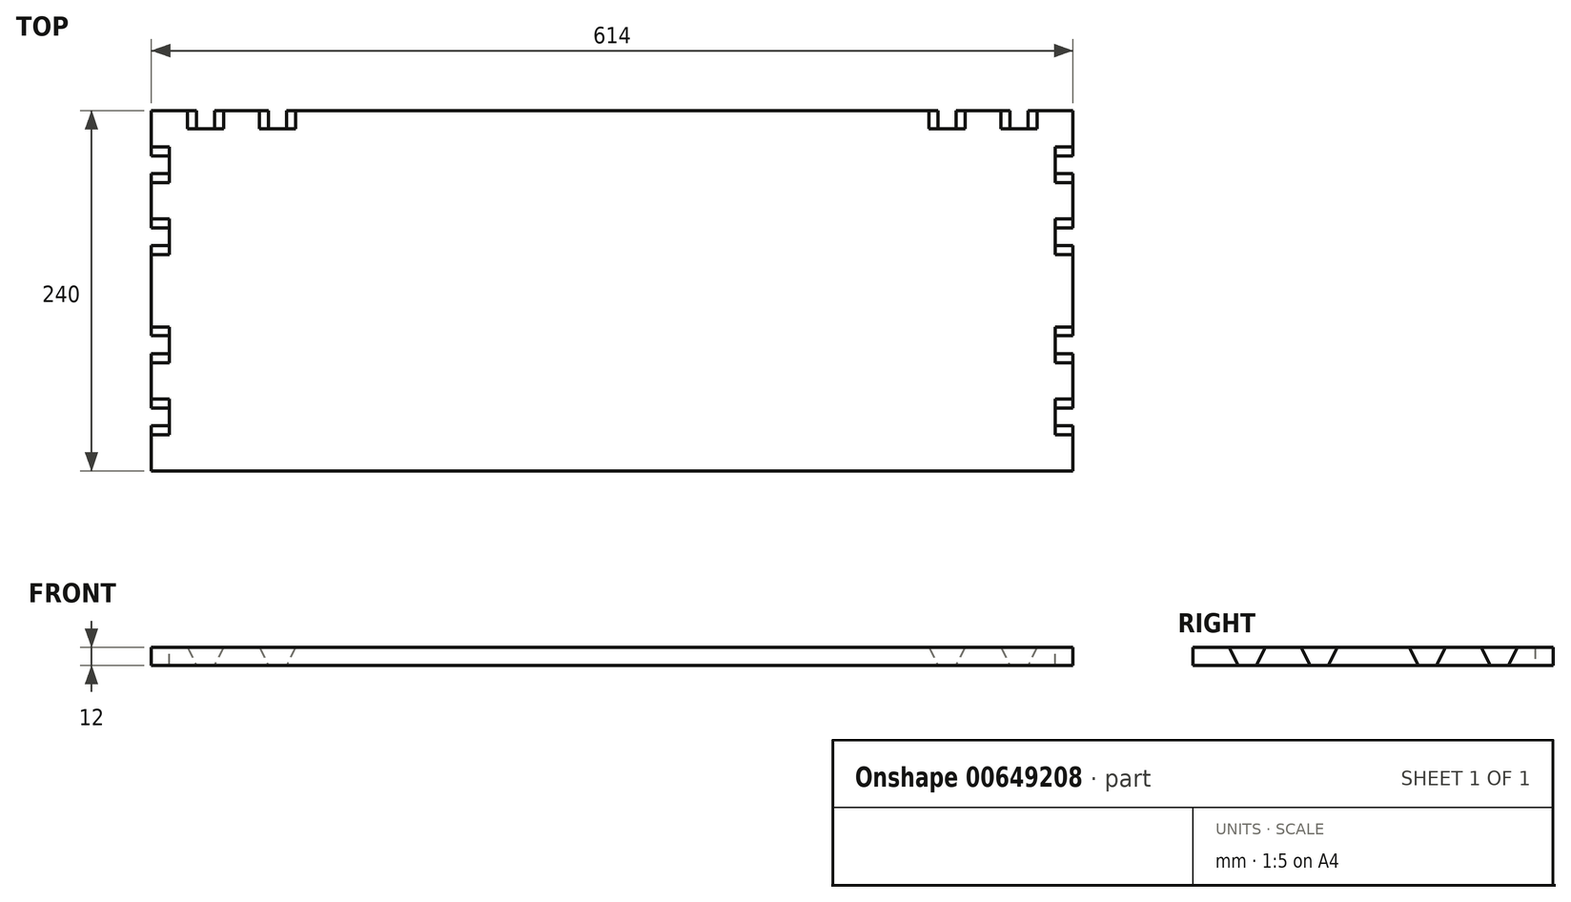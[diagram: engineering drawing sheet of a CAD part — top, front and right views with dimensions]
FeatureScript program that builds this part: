
annotation { "Feature Type Name" : "Feature", "Feature Type Description" : "" }
export const myFeature = defineFeature(function(context is Context, id is Id, definition is map)
    precondition{}
    {
        {
            var Q0;
            Q0=qCreatedBy(makeId("Top.planeOp"),FACE);
            var sketch = newSketch(context, id + "F0", { "sketchPlane" : qUnion([Q0])});
            skLineSegment(sketch, "E0.bottom", {"start": v(-307, 120) * mm, "end": v(307, 120) * mm});
            skLineSegment(sketch, "E0.top", {"start": v(-307, -120) * mm, "end": v(307, -120) * mm});
            skLineSegment(sketch, "E0.left", {"start": v(-307, 120) * mm, "end": v(-307, -120) * mm});
            skLineSegment(sketch, "E0.right", {"start": v(307, 120) * mm, "end": v(307, -120) * mm});
            skPoint(sketch, "E0.middle", {"position": v(0, 0) * mm});
            skLineSegment(sketch, "E1", {"start": v(-295, 120) * mm, "end": v(-295, -120) * mm, "construction": true});
            skLineSegment(sketch, "E2", {"start": v(-295, 116.5) * mm, "end": v(-307, 116.5) * mm, "construction": true});
            skLineSegment(sketch, "E3", {"start": v(295, 120) * mm, "end": v(295, -120) * mm, "construction": true});
            skLineSegment(sketch, "E4", {"start": v(307, 108.53) * mm, "end": v(295, 108.53) * mm, "construction": true});
            skLineSegment(sketch, "E5", {"start": v(-307, 108) * mm, "end": v(307, 108) * mm, "construction": true});
            skLineSegment(sketch, "E6", {"start": v(-289.12, 120) * mm, "end": v(-289.12, 108) * mm, "construction": true});
            skLineSegment(sketch, "E7.bottom", {"start": v(-307, -72) * mm, "end": v(-295, -72) * mm});
            skLineSegment(sketch, "E7.top", {"start": v(-307, -96) * mm, "end": v(-295, -96) * mm});
            skLineSegment(sketch, "E7.left", {"start": v(-307, -72) * mm, "end": v(-307, -96) * mm});
            skLineSegment(sketch, "E7.right", {"start": v(-295, -72) * mm, "end": v(-295, -96) * mm});
            skPoint(sketch, "E8", {"position": v(-307, -72) * mm});
            skPoint(sketch, "E9", {"position": v(-307, -96) * mm});
            skLineSegment(sketch, "E10", {"start": v(-301, -96) * mm, "end": v(-301, -120) * mm, "construction": true});
            skLineSegment(sketch, "E11", {"start": v(-307, -48) * mm, "end": v(-295, -48) * mm});
            skLineSegment(sketch, "E12", {"start": v(-295, -48) * mm, "end": v(-295, -24) * mm});
            skLineSegment(sketch, "E13", {"start": v(-295, -24) * mm, "end": v(-307, -24) * mm});
            skLineSegment(sketch, "E14", {"start": v(-307, -24) * mm, "end": v(-307, -48) * mm});
            skLineSegment(sketch, "E15", {"start": v(-301, -48) * mm, "end": v(-301, -72) * mm, "construction": true});
            skLineSegment(sketch, "E16", {"start": v(-307, 48) * mm, "end": v(-295, 48) * mm});
            skLineSegment(sketch, "E17", {"start": v(-295, 48) * mm, "end": v(-295, 24) * mm});
            skLineSegment(sketch, "E18", {"start": v(-295, 24) * mm, "end": v(-307, 24) * mm});
            skLineSegment(sketch, "E19", {"start": v(-307, 24) * mm, "end": v(-307, 48) * mm});
            skLineSegment(sketch, "E20.bottom", {"start": v(-307, 96) * mm, "end": v(-295, 96) * mm});
            skLineSegment(sketch, "E20.top", {"start": v(-307, 72) * mm, "end": v(-295, 72) * mm});
            skLineSegment(sketch, "E20.left", {"start": v(-307, 96) * mm, "end": v(-307, 72) * mm});
            skLineSegment(sketch, "E20.right", {"start": v(-295, 96) * mm, "end": v(-295, 72) * mm});
            skLineSegment(sketch, "E21", {"start": v(-301, 72) * mm, "end": v(-301, 48) * mm, "construction": true});
            skPoint(sketch, "E22.startSnap0", {"position": v(-301, 116.5) * mm});
            skLineSegment(sketch, "E23", {"start": v(-300.8, 120) * mm, "end": v(-300.8, 96) * mm, "construction": true});
            skLineSegment(sketch, "E24.bottom", {"start": v(295, -96) * mm, "end": v(307, -96) * mm});
            skLineSegment(sketch, "E24.top", {"start": v(295, -72) * mm, "end": v(307, -72) * mm});
            skLineSegment(sketch, "E24.left", {"start": v(295, -96) * mm, "end": v(295, -72) * mm});
            skLineSegment(sketch, "E24.right", {"start": v(307, -96) * mm, "end": v(307, -72) * mm});
            skLineSegment(sketch, "E25.bottom", {"start": v(295, -48) * mm, "end": v(307, -48) * mm});
            skLineSegment(sketch, "E25.top", {"start": v(295, -24) * mm, "end": v(307, -24) * mm});
            skLineSegment(sketch, "E25.left", {"start": v(295, -48) * mm, "end": v(295, -24) * mm});
            skLineSegment(sketch, "E25.right", {"start": v(307, -48) * mm, "end": v(307, -24) * mm});
            skLineSegment(sketch, "E26.bottom", {"start": v(295, 96) * mm, "end": v(307, 96) * mm});
            skLineSegment(sketch, "E26.top", {"start": v(295, 72) * mm, "end": v(307, 72) * mm});
            skLineSegment(sketch, "E26.left", {"start": v(295, 96) * mm, "end": v(295, 72) * mm});
            skLineSegment(sketch, "E26.right", {"start": v(307, 96) * mm, "end": v(307, 72) * mm});
            skLineSegment(sketch, "E27.bottom", {"start": v(295, 48) * mm, "end": v(307, 48) * mm});
            skLineSegment(sketch, "E27.top", {"start": v(295, 24) * mm, "end": v(307, 24) * mm});
            skLineSegment(sketch, "E27.left", {"start": v(295, 48) * mm, "end": v(295, 24) * mm});
            skLineSegment(sketch, "E27.right", {"start": v(307, 48) * mm, "end": v(307, 24) * mm});
            skLineSegment(sketch, "E28", {"start": v(301, -96) * mm, "end": v(301, -120) * mm, "construction": true});
            skLineSegment(sketch, "E29", {"start": v(300.92, 120) * mm, "end": v(300.92, 96) * mm, "construction": true});
            skLineSegment(sketch, "E30", {"start": v(301, -48) * mm, "end": v(301, -72) * mm, "construction": true});
            skLineSegment(sketch, "E31", {"start": v(301, 72) * mm, "end": v(301, 48) * mm, "construction": true});
            skLineSegment(sketch, "E32.bottom", {"start": v(-283, 120) * mm, "end": v(-259, 120) * mm});
            skLineSegment(sketch, "E32.top", {"start": v(-283, 108) * mm, "end": v(-259, 108) * mm});
            skLineSegment(sketch, "E32.left", {"start": v(-283, 120) * mm, "end": v(-283, 108) * mm});
            skLineSegment(sketch, "E32.right", {"start": v(-259, 120) * mm, "end": v(-259, 108) * mm});
            skLineSegment(sketch, "E33.bottom", {"start": v(-235, 120) * mm, "end": v(-211, 120) * mm});
            skLineSegment(sketch, "E33.top", {"start": v(-235, 108) * mm, "end": v(-211, 108) * mm});
            skLineSegment(sketch, "E33.left", {"start": v(-235, 120) * mm, "end": v(-235, 108) * mm});
            skLineSegment(sketch, "E33.right", {"start": v(-211, 120) * mm, "end": v(-211, 108) * mm});
            skLineSegment(sketch, "E34.bottom", {"start": v(283, 120) * mm, "end": v(259, 120) * mm});
            skLineSegment(sketch, "E34.top", {"start": v(283, 108) * mm, "end": v(259, 108) * mm});
            skLineSegment(sketch, "E34.left", {"start": v(283, 120) * mm, "end": v(283, 108) * mm});
            skLineSegment(sketch, "E34.right", {"start": v(259, 120) * mm, "end": v(259, 108) * mm});
            skLineSegment(sketch, "E35.bottom", {"start": v(235, 120) * mm, "end": v(211, 120) * mm});
            skLineSegment(sketch, "E35.top", {"start": v(235, 108) * mm, "end": v(211, 108) * mm});
            skLineSegment(sketch, "E35.left", {"start": v(235, 120) * mm, "end": v(235, 108) * mm});
            skLineSegment(sketch, "E35.right", {"start": v(211, 120) * mm, "end": v(211, 108) * mm});
            skLineSegment(sketch, "E36", {"start": v(307, 114.86) * mm, "end": v(283, 114.86) * mm, "construction": true});
            skLineSegment(sketch, "E37", {"start": v(259, 114) * mm, "end": v(235, 114) * mm, "construction": true});
            skLineSegment(sketch, "E38", {"start": v(-307, 113.75) * mm, "end": v(-283, 113.75) * mm, "construction": true});
            skLineSegment(sketch, "E39", {"start": v(-259, 114) * mm, "end": v(-235, 114) * mm, "construction": true});
            skLineSegment(sketch, "E40", {"start": v(-235, 111.04) * mm, "end": v(-211, 111.04) * mm, "construction": true});
            skLineSegment(sketch, "E41", {"start": v(235, 110.72) * mm, "end": v(211, 110.72) * mm, "construction": true});
            skLineSegment(sketch, "E42", {"start": v(259, 111.01) * mm, "end": v(283, 111.01) * mm, "construction": true});
            skSolve(sketch);
        }
        {
            var Q0;
            {var subQ4=sQuery(id+"F0.wireOp",EDGE,"E0.bottom");Q0=makeQuery(id+"F0.imprint","IMPRINT",FACE,{"disambiguationData":[TD([[makeQuery(id+"F0.imprint","IMPRINT",EDGE,{"derivedFrom":subQ4}),-1.0]])]});}
            extrude(context, id + "F1", {"entities" : qUnion([Q0]), "depth" : 12 * mm, "offsetDistance" : 25 * mm});
        }
        {
            var Q0;
            Q0=makeQuery(id+"F1.opExtrude","SWEPT_FACE",FACE,{"disambiguationData":[OSD([sQuery(id+"F0.wireOp",EDGE,"E7.right")])]});
            var sketch = newSketch(context, id + "F2", { "sketchPlane" : qUnion([Q0])});
            skLineSegment(sketch, "E43", {"start": v(72, 12) * mm, "end": v(72, 0) * mm});
            skLineSegment(sketch, "E44", {"start": v(72, 0) * mm, "end": v(78, 0) * mm});
            skLineSegment(sketch, "E45", {"start": v(78, 0) * mm, "end": v(72, 12) * mm});
            skLineSegment(sketch, "E46", {"start": v(96, 12) * mm, "end": v(96, 0) * mm});
            skLineSegment(sketch, "E47", {"start": v(96, 0) * mm, "end": v(90, 0) * mm});
            skLineSegment(sketch, "E48", {"start": v(90, 0) * mm, "end": v(96, 12) * mm});
            skSolve(sketch);
        }
        {
            var Q0;
            Q0 = qSketchRegion(id + "F2", true);
            extrude(context, id + "F3", {"entities" : qUnion([Q0]), "operationType" : NewBodyOperationType.ADD, "depth" : 12 * mm, "offsetDistance" : 25 * mm});
        }
        {
            var Q0;
            Q0=makeQuery(id+"F1.opExtrude","SWEPT_FACE",FACE,{"disambiguationData":[OSD([sQuery(id+"F0.wireOp",EDGE,"E12")])]});
            var sketch = newSketch(context, id + "F4", { "sketchPlane" : qUnion([Q0])});
            skLineSegment(sketch, "E49", {"start": v(24, 12) * mm, "end": v(30, 0) * mm});
            skLineSegment(sketch, "E50", {"start": v(30, 0) * mm, "end": v(24, 0) * mm});
            skLineSegment(sketch, "E51", {"start": v(24, 0) * mm, "end": v(24, 12) * mm});
            skLineSegment(sketch, "E52", {"start": v(48, 12) * mm, "end": v(48, 0) * mm});
            skLineSegment(sketch, "E53", {"start": v(48, 0) * mm, "end": v(42, 0) * mm});
            skLineSegment(sketch, "E54", {"start": v(42, 0) * mm, "end": v(48, 12) * mm});
            skSolve(sketch);
        }
        {
            var Q0;
            Q0 = qSketchRegion(id + "F4", true);
            extrude(context, id + "F5", {"entities" : qUnion([Q0]), "operationType" : NewBodyOperationType.ADD, "depth" : 12 * mm, "offsetDistance" : 25 * mm});
        }
        {
            var Q0;
            Q0=makeQuery(id+"F1.opExtrude","SWEPT_FACE",FACE,{"disambiguationData":[OSD([sQuery(id+"F0.wireOp",EDGE,"E17")])]});
            var sketch = newSketch(context, id + "F6", { "sketchPlane" : qUnion([Q0])});
            skLineSegment(sketch, "E55", {"start": v(-48, 12) * mm, "end": v(-42, 0) * mm});
            skLineSegment(sketch, "E56", {"start": v(-42, 0) * mm, "end": v(-48, 0) * mm});
            skLineSegment(sketch, "E57", {"start": v(-48, 0) * mm, "end": v(-48, 12) * mm});
            skLineSegment(sketch, "E58", {"start": v(-24, 12) * mm, "end": v(-24, 0) * mm});
            skLineSegment(sketch, "E59", {"start": v(-24, 0) * mm, "end": v(-30, 0) * mm});
            skLineSegment(sketch, "E60", {"start": v(-30, 0) * mm, "end": v(-24, 12) * mm});
            skSolve(sketch);
        }
        {
            var Q0;
            Q0 = qSketchRegion(id + "F6", true);
            extrude(context, id + "F7", {"entities" : qUnion([Q0]), "operationType" : NewBodyOperationType.ADD, "depth" : 12 * mm, "offsetDistance" : 25 * mm});
        }
        {
            var Q0;
            Q0=makeQuery(id+"F1.opExtrude","SWEPT_FACE",FACE,{"disambiguationData":[OSD([sQuery(id+"F0.wireOp",EDGE,"E20.right")])]});
            var sketch = newSketch(context, id + "F8", { "sketchPlane" : qUnion([Q0])});
            skLineSegment(sketch, "E61", {"start": v(-96, 12) * mm, "end": v(-90, 0) * mm});
            skLineSegment(sketch, "E62", {"start": v(-90, 0) * mm, "end": v(-96, 0) * mm});
            skLineSegment(sketch, "E63", {"start": v(-96, 0) * mm, "end": v(-96, 12) * mm});
            skLineSegment(sketch, "E64", {"start": v(-72, 12) * mm, "end": v(-72, 0) * mm});
            skLineSegment(sketch, "E65", {"start": v(-72, 0) * mm, "end": v(-78, 0) * mm});
            skLineSegment(sketch, "E66", {"start": v(-78, 0) * mm, "end": v(-72, 12) * mm});
            skSolve(sketch);
        }
        {
            var Q0;
            Q0 = qSketchRegion(id + "F8", true);
            extrude(context, id + "F9", {"entities" : qUnion([Q0]), "operationType" : NewBodyOperationType.ADD, "depth" : 12 * mm, "offsetDistance" : 25 * mm});
        }
        {
            var Q0;
            Q0=makeQuery(id+"F1.opExtrude","SWEPT_FACE",FACE,{"disambiguationData":[OSD([sQuery(id+"F0.wireOp",EDGE,"E24.left")])]});
            var sketch = newSketch(context, id + "F10", { "sketchPlane" : qUnion([Q0])});
            skLineSegment(sketch, "E67", {"start": v(-96, 12) * mm, "end": v(-90, 0) * mm});
            skLineSegment(sketch, "E68", {"start": v(-90, 0) * mm, "end": v(-96, 0) * mm});
            skLineSegment(sketch, "E69", {"start": v(-96, 0) * mm, "end": v(-96, 12) * mm});
            skLineSegment(sketch, "E70", {"start": v(-72, 12) * mm, "end": v(-72, 0) * mm});
            skLineSegment(sketch, "E71", {"start": v(-72, 0) * mm, "end": v(-78, 0) * mm});
            skLineSegment(sketch, "E72", {"start": v(-78, 0) * mm, "end": v(-72, 12) * mm});
            skSolve(sketch);
        }
        {
            var Q0;
            Q0 = qSketchRegion(id + "F10", true);
            extrude(context, id + "F11", {"entities" : qUnion([Q0]), "operationType" : NewBodyOperationType.ADD, "depth" : 12 * mm, "offsetDistance" : 25 * mm});
        }
        {
            var Q0;
            Q0=makeQuery(id+"F1.opExtrude","SWEPT_FACE",FACE,{"disambiguationData":[OSD([sQuery(id+"F0.wireOp",EDGE,"E25.left")])]});
            var sketch = newSketch(context, id + "F12", { "sketchPlane" : qUnion([Q0])});
            skLineSegment(sketch, "E73", {"start": v(-48, 12) * mm, "end": v(-42, 0) * mm});
            skLineSegment(sketch, "E74", {"start": v(-42, 0) * mm, "end": v(-48, 0) * mm});
            skLineSegment(sketch, "E75", {"start": v(-48, 0) * mm, "end": v(-48, 12) * mm});
            skLineSegment(sketch, "E76", {"start": v(-24, 12) * mm, "end": v(-24, 0) * mm});
            skLineSegment(sketch, "E77", {"start": v(-24, 0) * mm, "end": v(-30, 0) * mm});
            skLineSegment(sketch, "E78", {"start": v(-30, 0) * mm, "end": v(-24, 12) * mm});
            skSolve(sketch);
        }
        {
            var Q0;
            Q0 = qSketchRegion(id + "F12", true);
            extrude(context, id + "F13", {"entities" : qUnion([Q0]), "operationType" : NewBodyOperationType.ADD, "depth" : 12 * mm, "offsetDistance" : 25 * mm});
        }
        {
            var Q0;
            Q0=makeQuery(id+"F1.opExtrude","SWEPT_FACE",FACE,{"disambiguationData":[OSD([sQuery(id+"F0.wireOp",EDGE,"E27.left")])]});
            var sketch = newSketch(context, id + "F14", { "sketchPlane" : qUnion([Q0])});
            skLineSegment(sketch, "E79", {"start": v(24, 12) * mm, "end": v(30, 0) * mm});
            skLineSegment(sketch, "E80", {"start": v(30, 0) * mm, "end": v(24, 0) * mm});
            skLineSegment(sketch, "E81", {"start": v(24, 0) * mm, "end": v(24, 12) * mm});
            skLineSegment(sketch, "E82", {"start": v(48, 12) * mm, "end": v(48, 0) * mm});
            skLineSegment(sketch, "E83", {"start": v(48, 0) * mm, "end": v(42, 0) * mm});
            skLineSegment(sketch, "E84", {"start": v(42, 0) * mm, "end": v(48, 12) * mm});
            skSolve(sketch);
        }
        {
            var Q0;
            Q0 = qSketchRegion(id + "F14", true);
            extrude(context, id + "F15", {"entities" : qUnion([Q0]), "operationType" : NewBodyOperationType.ADD, "depth" : 12 * mm, "offsetDistance" : 25 * mm});
        }
        {
            var Q0;
            Q0=makeQuery(id+"F1.opExtrude","SWEPT_FACE",FACE,{"disambiguationData":[OSD([sQuery(id+"F0.wireOp",EDGE,"E26.left")])]});
            var sketch = newSketch(context, id + "F16", { "sketchPlane" : qUnion([Q0])});
            skLineSegment(sketch, "E85", {"start": v(72, 12) * mm, "end": v(78, 0) * mm});
            skLineSegment(sketch, "E86", {"start": v(78, 0) * mm, "end": v(72, 0) * mm});
            skLineSegment(sketch, "E87", {"start": v(72, 0) * mm, "end": v(72, 12) * mm});
            skLineSegment(sketch, "E88", {"start": v(96, 12) * mm, "end": v(96, 0) * mm});
            skLineSegment(sketch, "E89", {"start": v(96, 0) * mm, "end": v(90, 0) * mm});
            skLineSegment(sketch, "E90", {"start": v(90, 0) * mm, "end": v(96, 12) * mm});
            skSolve(sketch);
        }
        {
            var Q0;
            Q0 = qSketchRegion(id + "F16", true);
            extrude(context, id + "F17", {"entities" : qUnion([Q0]), "operationType" : NewBodyOperationType.ADD, "depth" : 12 * mm, "offsetDistance" : 25 * mm});
        }
        {
            var Q0;
            Q0=makeQuery(id+"F1.opExtrude","SWEPT_FACE",FACE,{"disambiguationData":[OSD([sQuery(id+"F0.wireOp",EDGE,"E34.top")])]});
            var sketch = newSketch(context, id + "F18", { "sketchPlane" : qUnion([Q0])});
            skLineSegment(sketch, "E91", {"start": v(-283, 12) * mm, "end": v(-277, 0) * mm});
            skLineSegment(sketch, "E92", {"start": v(-277, 0) * mm, "end": v(-283, 0) * mm});
            skLineSegment(sketch, "E93", {"start": v(-283, 0) * mm, "end": v(-283, 12) * mm});
            skLineSegment(sketch, "E94", {"start": v(-259, 12) * mm, "end": v(-265, 0) * mm});
            skLineSegment(sketch, "E95", {"start": v(-265, 0) * mm, "end": v(-259, 0) * mm});
            skLineSegment(sketch, "E96", {"start": v(-259, 0) * mm, "end": v(-259, 12) * mm});
            skSolve(sketch);
        }
        {
            var Q0;
            Q0 = qSketchRegion(id + "F18", true);
            extrude(context, id + "F19", {"entities" : qUnion([Q0]), "operationType" : NewBodyOperationType.ADD, "depth" : 12 * mm, "offsetDistance" : 25 * mm});
        }
        {
            var Q0;
            Q0=makeQuery(id+"F1.opExtrude","SWEPT_FACE",FACE,{"disambiguationData":[OSD([sQuery(id+"F0.wireOp",EDGE,"E35.top")])]});
            var sketch = newSketch(context, id + "F20", { "sketchPlane" : qUnion([Q0])});
            skLineSegment(sketch, "E97", {"start": v(-235, 12) * mm, "end": v(-229, 0) * mm});
            skLineSegment(sketch, "E98", {"start": v(-229, 0) * mm, "end": v(-235, 0) * mm});
            skLineSegment(sketch, "E99", {"start": v(-235, 0) * mm, "end": v(-235, 12) * mm});
            skLineSegment(sketch, "E100", {"start": v(-211, 12) * mm, "end": v(-217, 0) * mm});
            skLineSegment(sketch, "E101", {"start": v(-217, 0) * mm, "end": v(-211, 0) * mm});
            skLineSegment(sketch, "E102", {"start": v(-211, 0) * mm, "end": v(-211, 12) * mm});
            skSolve(sketch);
        }
        {
            var Q0;
            Q0 = qSketchRegion(id + "F20", true);
            extrude(context, id + "F21", {"entities" : qUnion([Q0]), "operationType" : NewBodyOperationType.ADD, "depth" : 12 * mm, "offsetDistance" : 25 * mm});
        }
        {
            var Q0;
            Q0=makeQuery(id+"F1.opExtrude","SWEPT_FACE",FACE,{"disambiguationData":[OSD([sQuery(id+"F0.wireOp",EDGE,"E33.top")])]});
            var sketch = newSketch(context, id + "F22", { "sketchPlane" : qUnion([Q0])});
            skLineSegment(sketch, "E103", {"start": v(211, 12) * mm, "end": v(217, 0) * mm});
            skLineSegment(sketch, "E104", {"start": v(217, 0) * mm, "end": v(211, 0) * mm});
            skLineSegment(sketch, "E105", {"start": v(211, 0) * mm, "end": v(211, 12) * mm});
            skLineSegment(sketch, "E106", {"start": v(235, 12) * mm, "end": v(229, 0) * mm});
            skLineSegment(sketch, "E107", {"start": v(229, 0) * mm, "end": v(235, 0) * mm});
            skLineSegment(sketch, "E108", {"start": v(235, 0) * mm, "end": v(235, 12) * mm});
            skSolve(sketch);
        }
        {
            var Q0;
            Q0 = qSketchRegion(id + "F22", true);
            extrude(context, id + "F23", {"entities" : qUnion([Q0]), "operationType" : NewBodyOperationType.ADD, "depth" : 12 * mm, "offsetDistance" : 25 * mm});
        }
        {
            var Q0;
            Q0=makeQuery(id+"F1.opExtrude","SWEPT_FACE",FACE,{"disambiguationData":[OSD([sQuery(id+"F0.wireOp",EDGE,"E32.top")])]});
            var sketch = newSketch(context, id + "F24", { "sketchPlane" : qUnion([Q0])});
            skLineSegment(sketch, "E109", {"start": v(259, 12) * mm, "end": v(265, 0) * mm});
            skLineSegment(sketch, "E110", {"start": v(265, 0) * mm, "end": v(259, 0) * mm});
            skLineSegment(sketch, "E111", {"start": v(259, 0) * mm, "end": v(259, 12) * mm});
            skLineSegment(sketch, "E112", {"start": v(283, 12) * mm, "end": v(277, 0) * mm});
            skLineSegment(sketch, "E113", {"start": v(277, 0) * mm, "end": v(283, 0) * mm});
            skLineSegment(sketch, "E114", {"start": v(283, 0) * mm, "end": v(283, 12) * mm});
            skSolve(sketch);
        }
        {
            var Q0;
            Q0 = qSketchRegion(id + "F24", true);
            extrude(context, id + "F25", {"entities" : qUnion([Q0]), "operationType" : NewBodyOperationType.ADD, "depth" : 12 * mm, "offsetDistance" : 25 * mm});
        }
    });
